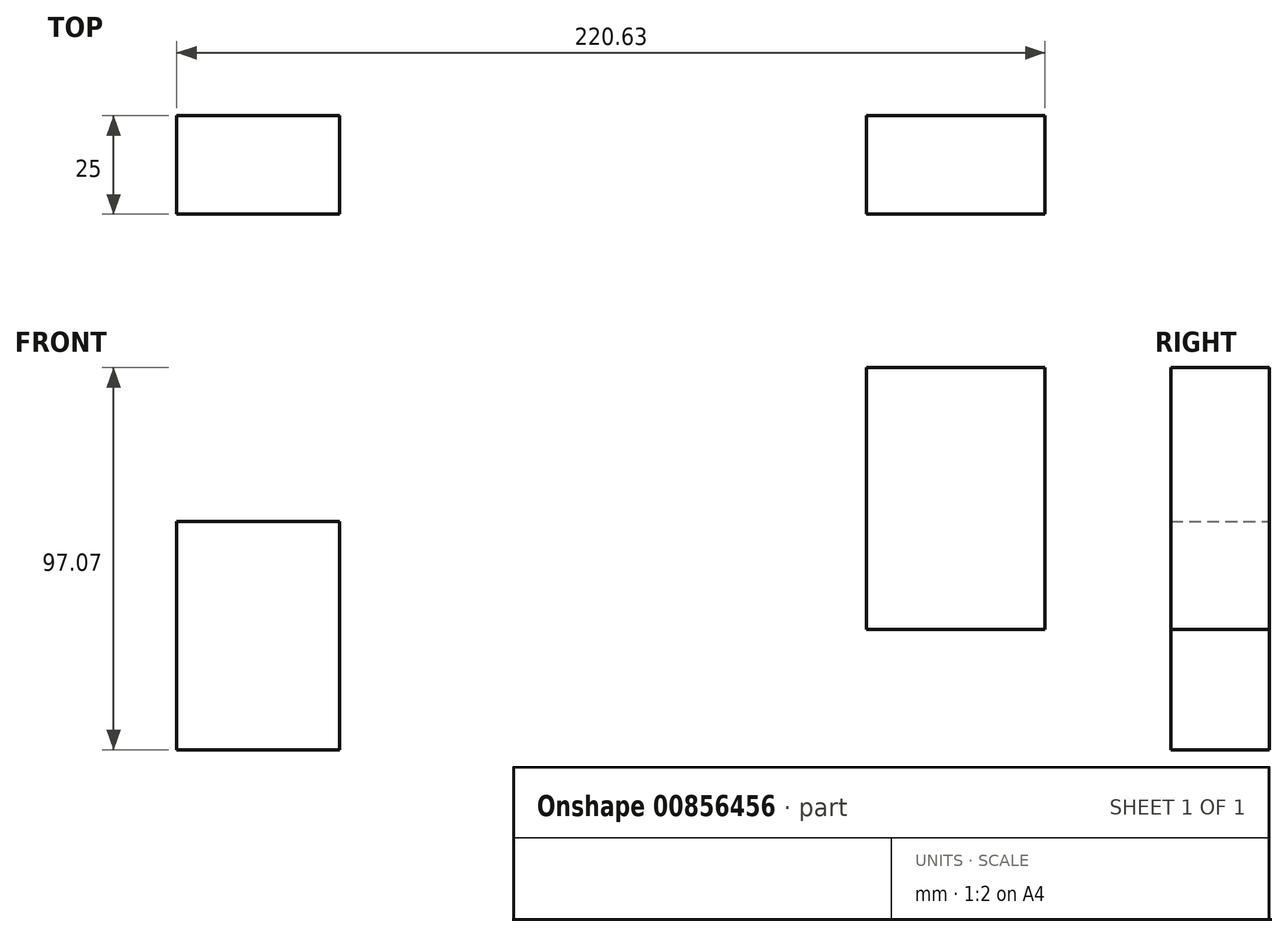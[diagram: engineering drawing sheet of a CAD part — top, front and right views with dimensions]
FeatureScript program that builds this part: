
annotation { "Feature Type Name" : "Feature", "Feature Type Description" : "" }
export const myFeature = defineFeature(function(context is Context, id is Id, definition is map)
    precondition{}
    {
        {
            var Q0;
            Q0=qCreatedBy(makeId("Front.planeOp"),FACE);
            var sketch = newSketch(context, id + "F0", { "sketchPlane" : qUnion([Q0])});
            skLineSegment(sketch, "E0.bottom", {"start": v(-145.86, -4.56) * mm, "end": v(-104.48, -4.56) * mm});
            skLineSegment(sketch, "E0.top", {"start": v(-145.86, 53.45) * mm, "end": v(-104.48, 53.45) * mm});
            skLineSegment(sketch, "E0.left", {"start": v(-145.86, -4.56) * mm, "end": v(-145.86, 53.45) * mm});
            skLineSegment(sketch, "E0.right", {"start": v(-104.48, -4.56) * mm, "end": v(-104.48, 53.45) * mm});
            skPoint(sketch, "E0.middle", {"position": v(-125.17, 24.45) * mm});
            skLineSegment(sketch, "E1.bottom", {"start": v(29.37, 26) * mm, "end": v(74.77, 26) * mm});
            skLineSegment(sketch, "E1.top", {"start": v(29.37, 92.51) * mm, "end": v(74.77, 92.51) * mm});
            skLineSegment(sketch, "E1.left", {"start": v(29.37, 26) * mm, "end": v(29.37, 92.51) * mm});
            skLineSegment(sketch, "E1.right", {"start": v(74.77, 26) * mm, "end": v(74.77, 92.51) * mm});
            skPoint(sketch, "E1.middle", {"position": v(52.07, 59.26) * mm});
            skLineSegment(sketch, "E2", {"start": v(-50.4, 0) * mm, "end": v(-16.36, -64.3) * mm});
            skLineSegment(sketch, "E3", {"start": v(65.09, -88.52) * mm, "end": v(126.17, 2.88) * mm});
            skSolve(sketch);
        }
        {
            var Q0;
            Q0=makeQuery(id+"F0.imprint","IMPRINT",FACE,{"disambiguationData":[TD([[makeQuery(id+"F0.imprint","IMPRINT",EDGE,{"derivedFrom":sQuery(id+"F0.wireOp",EDGE,"E0.bottom")}),1.0]])]});
            var Q1;
            Q1=makeQuery(id+"F0.imprint","IMPRINT",FACE,{"disambiguationData":[TD([[makeQuery(id+"F0.imprint","IMPRINT",EDGE,{"derivedFrom":sQuery(id+"F0.wireOp",EDGE,"E1.bottom")}),1.0]])]});
            extrude(context, id + "F1", {"entities" : qUnion([Q0, Q1]), "depth" : 25 * mm, "offsetDistance" : 25 * mm});
        }
        {
            var Q0;
            Q0=sQuery(id+"F0.wireOp",EDGE,"E2");
            var Q1;
            Q1=sQuery(id+"F0.wireOp",EDGE,"E3");
            extrude(context, id + "F2", {"bodyType" : ToolBodyType.SURFACE, "surfaceEntities" : qUnion([Q0, Q1]), "depth" : 25 * mm, "offsetDistance" : 25 * mm});
        }
    });
